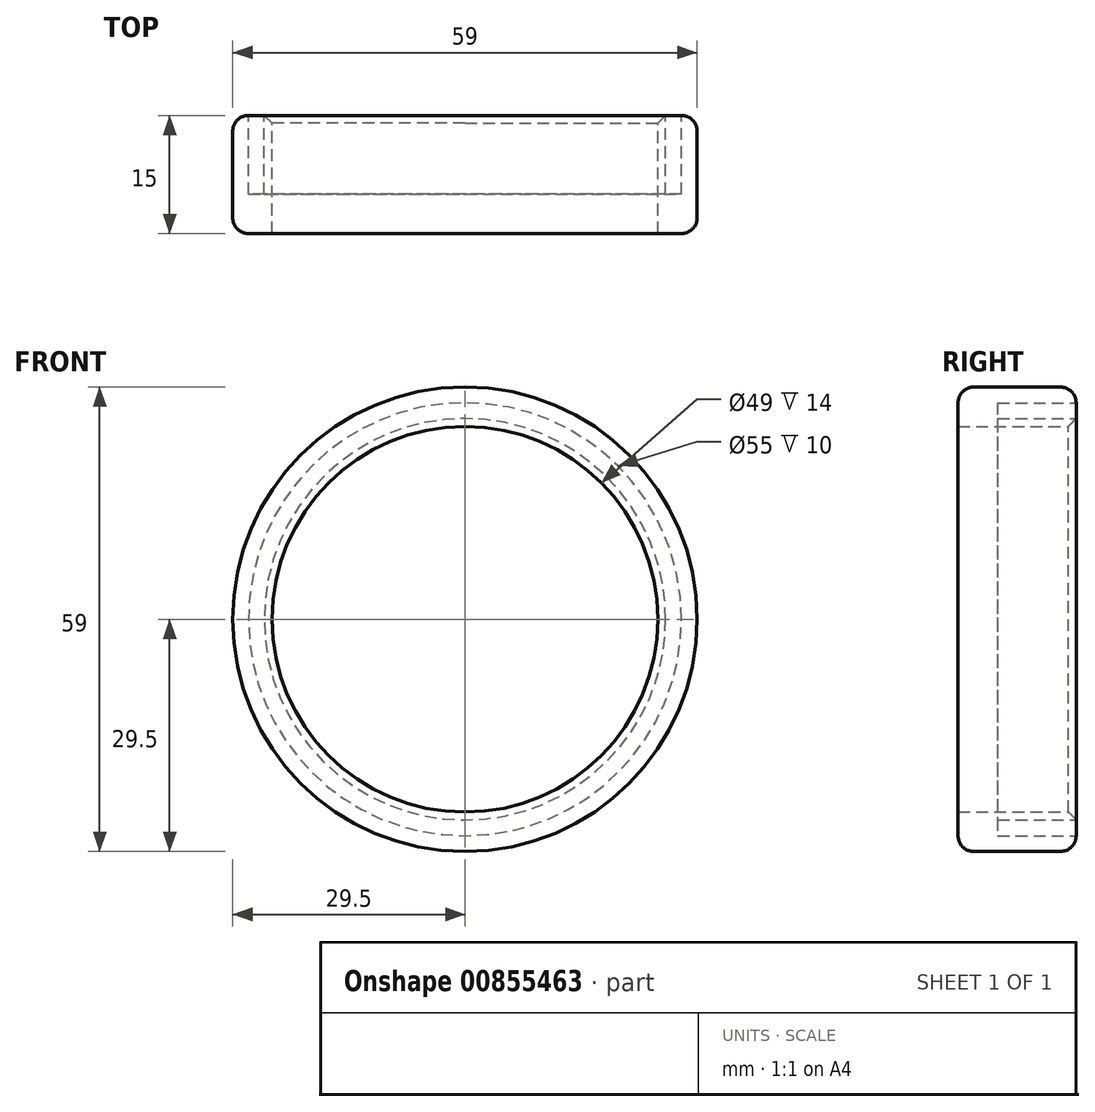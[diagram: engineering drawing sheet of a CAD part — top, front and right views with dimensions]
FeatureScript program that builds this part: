
annotation { "Feature Type Name" : "Feature", "Feature Type Description" : "" }
export const myFeature = defineFeature(function(context is Context, id is Id, definition is map)
    precondition{}
    {
        {
            var Q0;
            Q0=qCreatedBy(makeId("Top.planeOp"),FACE);
            var sketch = newSketch(context, id + "F0", { "sketchPlane" : qUnion([Q0])});
            skLineSegment(sketch, "E0", {"start": v(-24.5, 14.3) * mm, "end": v(-24.5, 0) * mm});
            skLineSegment(sketch, "E1", {"start": v(-24.5, 0) * mm, "end": v(-29.5, 0) * mm});
            skLineSegment(sketch, "E2", {"start": v(-29.5, 0) * mm, "end": v(-29.5, 15) * mm});
            skLineSegment(sketch, "E3", {"start": v(-29.5, 15) * mm, "end": v(-27.5, 15) * mm});
            skLineSegment(sketch, "E4", {"start": v(-27.5, 15) * mm, "end": v(-27.5, 5) * mm});
            skLineSegment(sketch, "E5", {"start": v(-27.5, 5) * mm, "end": v(-25.5, 5) * mm});
            skLineSegment(sketch, "E6", {"start": v(-25.5, 5) * mm, "end": v(-25.5, 15) * mm});
            skLineSegment(sketch, "E7", {"start": v(-25.5, 15) * mm, "end": v(-24.5, 15) * mm});
            skLineSegment(sketch, "E8", {"start": v(-24.5, 15) * mm, "end": v(-24.5, 0) * mm});
            skLineSegment(sketch, "E9", {"start": v(0, 28.28) * mm, "end": v(0, -13.17) * mm});
            skSolve(sketch);
        }
        {
            var Q0;
            Q0 = qSketchRegion(id + "F0", true);
            var Q1;
            Q1=sQuery(id+"F0.wireOp",EDGE,"E9");
            revolve(context, id + "F1", {"surfaceOperationType" : NewSurfaceOperationType.NEW, "entities" : qUnion([Q0]), "axis" : qUnion([Q1]), "revolveType" : RevolveType.FULL});
        }
        {
            var Q0;
            Q0=makeQuery(id+"F1.opRevolve","SWEPT_EDGE",EDGE,{"disambiguationData":[OSD([sQuery(id+"F0.wireOp",EDGE,"E2"),sQuery(id+"F0.wireOp",EDGE,"E3")])]});
            var Q1;
            Q1=makeQuery(id+"F1.opRevolve","SWEPT_EDGE",EDGE,{"disambiguationData":[OSD([sQuery(id+"F0.wireOp",EDGE,"E1"),sQuery(id+"F0.wireOp",EDGE,"E2")])]});
            fillet(context, id + "F2", {"entities" : qUnion([Q0, Q1]), "radius" : 2 * mm, "tangentPropagation" : true, "allowEdgeOverflow" : false});
        }
        {
            var Q0;
            Q0=makeQuery(id+"F1.opRevolve","SWEPT_EDGE",EDGE,{"disambiguationData":[OSD([sQuery(id+"F0.wireOp",EDGE,"E7"),sQuery(id+"F0.wireOp",EDGE,"E8")])]});
            chamfer(context, id + "F3", {"entities" : qUnion([Q0]), "width" : 1 * mm, "tangentPropagation" : true});
        }
    });
